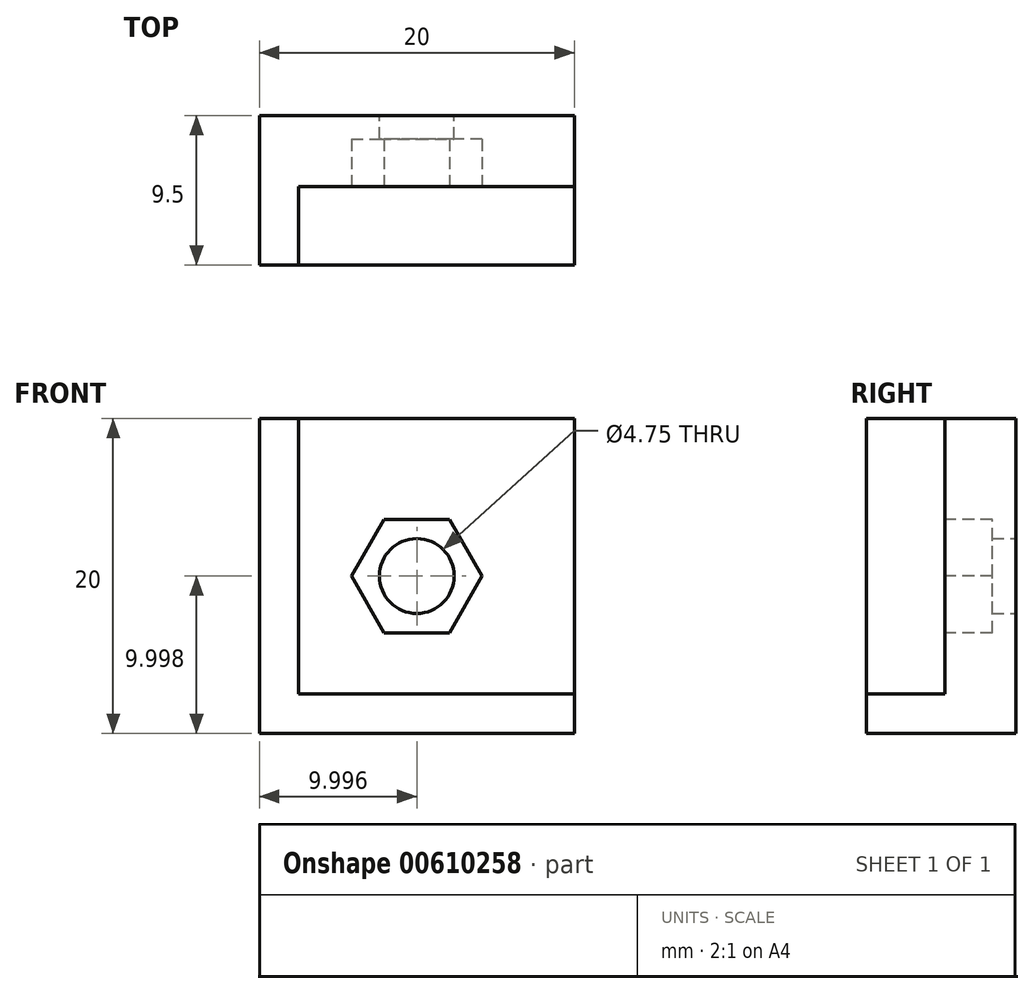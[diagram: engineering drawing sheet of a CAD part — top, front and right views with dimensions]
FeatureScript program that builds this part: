
annotation { "Feature Type Name" : "Feature", "Feature Type Description" : "" }
export const myFeature = defineFeature(function(context is Context, id is Id, definition is map)
    precondition{}
    {
        {
            var Q0;
            Q0=qCreatedBy(makeId("Front.planeOp"),FACE);
            var sketch = newSketch(context, id + "F0", { "sketchPlane" : qUnion([Q0])});
            skLineSegment(sketch, "E0.bottom", {"start": v(-7.84, 13.83) * mm, "end": v(12.16, 13.83) * mm});
            skLineSegment(sketch, "E0.top", {"start": v(-7.84, -6.17) * mm, "end": v(12.16, -6.17) * mm});
            skLineSegment(sketch, "E0.left", {"start": v(-7.84, 13.83) * mm, "end": v(-7.84, -6.17) * mm});
            skLineSegment(sketch, "E0.right", {"start": v(12.16, 13.83) * mm, "end": v(12.16, -6.17) * mm});
            skCircle(sketch, "E1", {"center": v(2.16, 3.83) * mm, "radius": 2.38 * mm});
            skSolve(sketch);
        }
        {
            var Q0;
            Q0=makeQuery(id+"F0.imprint","IMPRINT",FACE,{"disambiguationData":[TD([[makeQuery(id+"F0.imprint","IMPRINT",EDGE,{"derivedFrom":sQuery(id+"F0.wireOp",EDGE,"E0.bottom")}),-1.0]])]});
            extrude(context, id + "F1", {"entities" : qUnion([Q0]), "depth" : 4.5 * mm, "offsetDistance" : 25.4 * mm});
        }
        {
            var Q0;
            Q0=makeQuery(id+"F1.opExtrude","CAP_FACE",FACE,{"disambiguationData":[OSD([sQuery(id+"F0.wireOp",EDGE,"E0.bottom"),sQuery(id+"F0.wireOp",EDGE,"E0.top"),sQuery(id+"F0.wireOp",EDGE,"E0.left"),sQuery(id+"F0.wireOp",EDGE,"E0.right"),sQuery(id+"F0.wireOp",EDGE,"e61c1b9d-ad0a-4759-b9ae-b7011fac5f62.0"),sQuery(id+"F0.wireOp",EDGE,"e61c1b9d-ad0a-4759-b9ae-b7011fac5f62.1"),sQuery(id+"F0.wireOp",EDGE,"e61c1b9d-ad0a-4759-b9ae-b7011fac5f62.2"),sQuery(id+"F0.wireOp",EDGE,"e61c1b9d-ad0a-4759-b9ae-b7011fac5f62.3"),sQuery(id+"F0.wireOp",EDGE,"e61c1b9d-ad0a-4759-b9ae-b7011fac5f62.4"),sQuery(id+"F0.wireOp",EDGE,"e61c1b9d-ad0a-4759-b9ae-b7011fac5f62.5")])],"isStart":false});
            var sketch = newSketch(context, id + "F2", { "sketchPlane" : qUnion([Q0])});
            skLineSegment(sketch, "E2", {"start": v(-7.84, 13.83) * mm, "end": v(-5.34, 13.83) * mm});
            skLineSegment(sketch, "E3", {"start": v(-5.34, 13.83) * mm, "end": v(-5.34, -3.67) * mm});
            skLineSegment(sketch, "E4", {"start": v(-5.34, -3.67) * mm, "end": v(12.16, -3.67) * mm});
            skLineSegment(sketch, "E5", {"start": v(12.16, -3.67) * mm, "end": v(12.16, -6.17) * mm});
            skLineSegment(sketch, "E6", {"start": v(12.16, -6.17) * mm, "end": v(-7.84, -6.17) * mm});
            skLineSegment(sketch, "E7", {"start": v(-7.84, -6.17) * mm, "end": v(-7.84, 13.83) * mm});
            skSolve(sketch);
        }
        {
            var Q0;
            Q0=makeQuery(id+"F2.imprint","IMPRINT",FACE,{"disambiguationData":[TD([[makeQuery(id+"F2.imprint","IMPRINT",EDGE,{"derivedFrom":sQuery(id+"F2.wireOp",EDGE,"E2")}),-1.0]])]});
            extrude(context, id + "F3", {"entities" : qUnion([Q0]), "operationType" : NewBodyOperationType.ADD, "depth" : 5 * mm, "offsetDistance" : 25.4 * mm});
        }
        {
            var Q0;
            Q0=makeQuery(id+"F1.opExtrude","CAP_FACE",FACE,{"disambiguationData":[OSD([sQuery(id+"F0.wireOp",EDGE,"E0.bottom"),sQuery(id+"F0.wireOp",EDGE,"E0.top"),sQuery(id+"F0.wireOp",EDGE,"E0.left"),sQuery(id+"F0.wireOp",EDGE,"E0.right"),sQuery(id+"F0.wireOp",EDGE,"E1")])],"isStart":false});
            var sketch = newSketch(context, id + "F4", { "sketchPlane" : qUnion([Q0])});
            skCircle(sketch, "E8.cCircle", {"center": v(2.16, 3.83) * mm, "radius": 3.6 * mm, "construction": true});
            skLineSegment(sketch, "E8.0", {"start": v(-2, 3.83) * mm, "end": v(0.08, 7.43) * mm});
            skLineSegment(sketch, "E8.1", {"start": v(0.08, 7.43) * mm, "end": v(4.23, 7.43) * mm});
            skLineSegment(sketch, "E8.2", {"start": v(4.23, 7.43) * mm, "end": v(6.31, 3.83) * mm});
            skLineSegment(sketch, "E8.3", {"start": v(6.31, 3.83) * mm, "end": v(4.23, 0.23) * mm});
            skLineSegment(sketch, "E8.4", {"start": v(4.23, 0.23) * mm, "end": v(0.08, 0.23) * mm});
            skLineSegment(sketch, "E8.5", {"start": v(0.08, 0.23) * mm, "end": v(-2, 3.83) * mm});
            skPoint(sketch, "E8.0.midPoint", {"position": v(-0.96, 5.63) * mm});
            skSolve(sketch);
        }
        {
            var Q0;
            Q0=makeQuery(id+"F4.imprint","IMPRINT",FACE,{"disambiguationData":[TD([[makeQuery(id+"F4.imprint","IMPRINT",EDGE,{"derivedFrom":sQuery(id+"F4.wireOp",EDGE,"E8.0")}),-1.0]])]});
            extrude(context, id + "F5", {"entities" : qUnion([Q0]), "operationType" : NewBodyOperationType.REMOVE, "oppositeDirection" : true, "depth" : 3 * mm, "offsetDistance" : 25.4 * mm});
        }
    });
